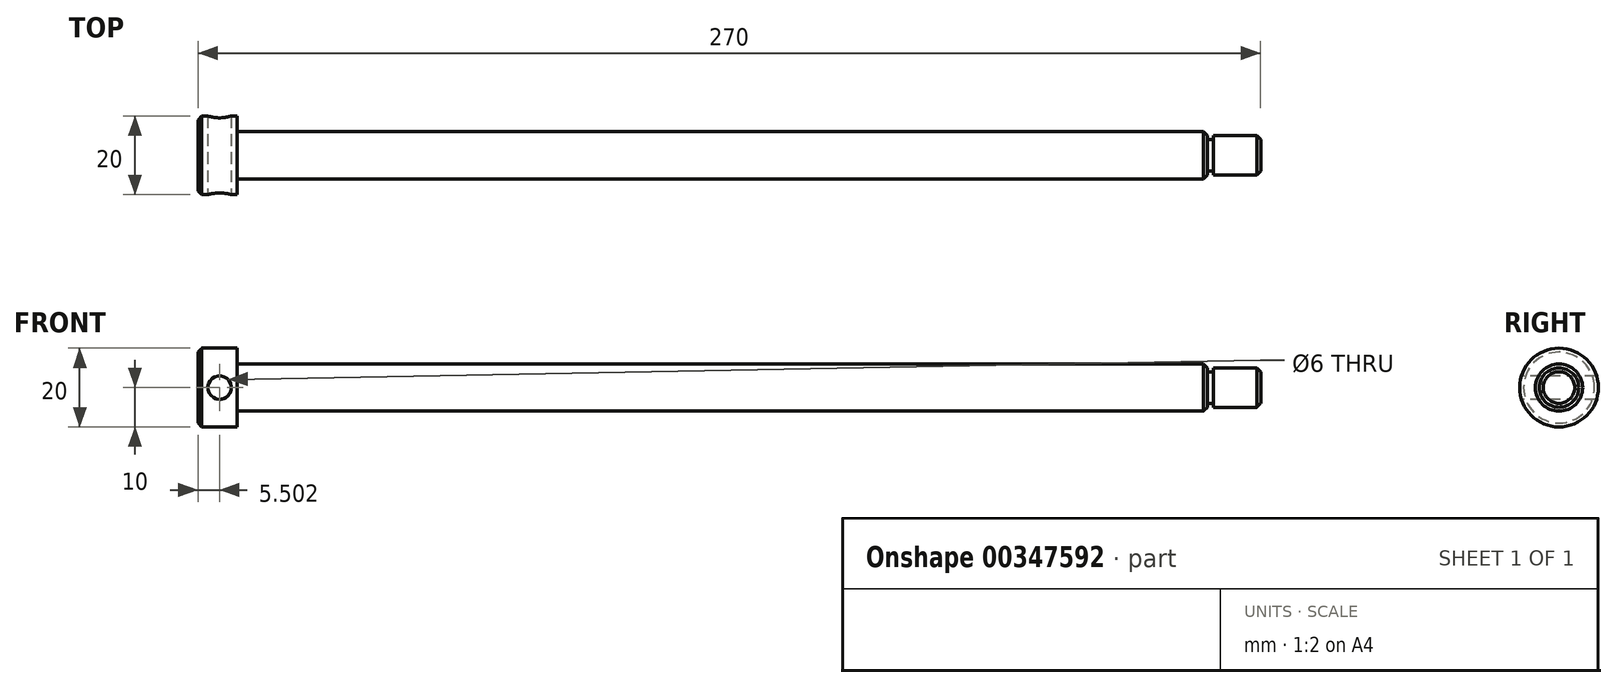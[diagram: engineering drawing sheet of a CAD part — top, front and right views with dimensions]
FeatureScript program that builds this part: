
annotation { "Feature Type Name" : "Feature", "Feature Type Description" : "" }
export const myFeature = defineFeature(function(context is Context, id is Id, definition is map)
    precondition{}
    {
        {
            var Q0;
            Q0=qCreatedBy(makeId("Front.planeOp"),FACE);
            var sketch = newSketch(context, id + "F0", { "sketchPlane" : qUnion([Q0])});
            skLineSegment(sketch, "E0", {"start": v(-103.15, 0) * mm, "end": v(166.85, 0) * mm});
            skLineSegment(sketch, "E1.0", {"start": v(-103.15, 10) * mm, "end": v(-93.15, 10) * mm});
            skLineSegment(sketch, "E2.0", {"start": v(-93.15, 6) * mm, "end": v(153.35, 6) * mm});
            skLineSegment(sketch, "E3", {"start": v(166.85, 5) * mm, "end": v(166.85, 0) * mm});
            skLineSegment(sketch, "E4.0", {"start": v(154.85, 5) * mm, "end": v(154.85, 4) * mm});
            skLineSegment(sketch, "E5", {"start": v(-103.15, 0) * mm, "end": v(-103.15, 10) * mm});
            skLineSegment(sketch, "E6.0", {"start": v(-93.15, 6) * mm, "end": v(-93.15, 10) * mm});
            skLineSegment(sketch, "E7.0", {"start": v(153.35, 6) * mm, "end": v(153.35, 4) * mm});
            skLineSegment(sketch, "E8.trimOffspring", {"start": v(153.35, 4) * mm, "end": v(154.85, 4) * mm});
            skLineSegment(sketch, "E9.trimOffspring", {"start": v(154.85, 5) * mm, "end": v(166.85, 5) * mm});
            skSolve(sketch);
        }
        {
            var Q0;
            Q0=makeQuery(id+"F0.imprint","IMPRINT",FACE,{"disambiguationData":[TD([[makeQuery(id+"F0.imprint","IMPRINT",EDGE,{"derivedFrom":sQuery(id+"F0.wireOp",EDGE,"E0")}),1.0]])]});
            var Q1;
            Q1=sQuery(id+"F0.wireOp",EDGE,"E0");
            revolve(context, id + "F1", {"entities" : qUnion([Q0]), "axis" : qUnion([Q1]), "revolveType" : RevolveType.FULL});
        }
        {
            var Q0;
            Q0=makeQuery(id+"F1.opRevolve","SWEPT_EDGE",EDGE,{"disambiguationData":[OSD([sQuery(id+"F0.wireOp",EDGE,"E2.0"),sQuery(id+"F0.wireOp",EDGE,"E7.0")])]});
            var Q1;
            Q1=makeQuery(id+"F1.opRevolve","SWEPT_EDGE",EDGE,{"disambiguationData":[OSD([sQuery(id+"F0.wireOp",EDGE,"E1.0"),sQuery(id+"F0.wireOp",EDGE,"E5")])]});
            var Q2;
            Q2=makeQuery(id+"F1.opRevolve","SWEPT_EDGE",EDGE,{"disambiguationData":[OSD([sQuery(id+"F0.wireOp",EDGE,"E3"),sQuery(id+"F0.wireOp",EDGE,"E9.trimOffspring")])]});
            var Q3;
            Q3=makeQuery(id+"F1.opRevolve","SWEPT_EDGE",EDGE,{"disambiguationData":[OSD([sQuery(id+"F0.wireOp",EDGE,"E2.0"),sQuery(id+"F0.wireOp",EDGE,"E7.0")])]});
            chamfer(context, id + "F2", {"entities" : qUnion([Q0, Q1, Q2, Q3]), "width" : 1 * mm, "tangentPropagation" : true});
        }
        {
            var Q0;
            Q0=qCreatedBy(makeId("Front.planeOp"),FACE);
            cPlane(context, id + "F3", {"entities" : qUnion([Q0]), "cplaneType" : CPlaneType.OFFSET, "offset" : 25 * mm, "width" : 150 * mm, "height" : 150 * mm});
        }
        {
            var Q0;
            Q0=qCreatedBy(id+"F3.planeOp",FACE);
            var sketch = newSketch(context, id + "F4", { "sketchPlane" : qUnion([Q0])});
            skLineSegment(sketch, "E10.0", {"start": v(-102.15, 10) * mm, "end": v(-102.15, -10) * mm, "construction": true});
            skLineSegment(sketch, "E11.0", {"start": v(-93.15, -10) * mm, "end": v(-93.15, 10) * mm, "construction": true});
            skLineSegment(sketch, "E12", {"start": v(-102.15, 10) * mm, "end": v(-93.15, 10) * mm, "construction": true});
            skLineSegment(sketch, "E13", {"start": v(-93.15, -10) * mm, "end": v(-102.15, -10) * mm, "construction": true});
            skLineSegment(sketch, "E14", {"start": v(-97.65, 11.82) * mm, "end": v(-97.65, -12.94) * mm, "construction": true});
            skLineSegment(sketch, "E15", {"start": v(-102.15, 0) * mm, "end": v(-89.85, 0) * mm, "construction": true});
            skCircle(sketch, "E16", {"center": v(-97.65, 0) * mm, "radius": 3 * mm});
            skSolve(sketch);
        }
        {
            var Q0;
            Q0=makeQuery(id+"F4.imprint","IMPRINT",FACE,{"disambiguationData":[TD([[makeQuery(id+"F4.imprint","IMPRINT",EDGE,{"derivedFrom":sQuery(id+"F4.wireOp",EDGE,"E16")}),1.0]])]});
            extrude(context, id + "F5", {"entities" : qUnion([Q0]), "operationType" : NewBodyOperationType.REMOVE, "oppositeDirection" : true, "depth" : 39.4 * mm});
        }
    });
